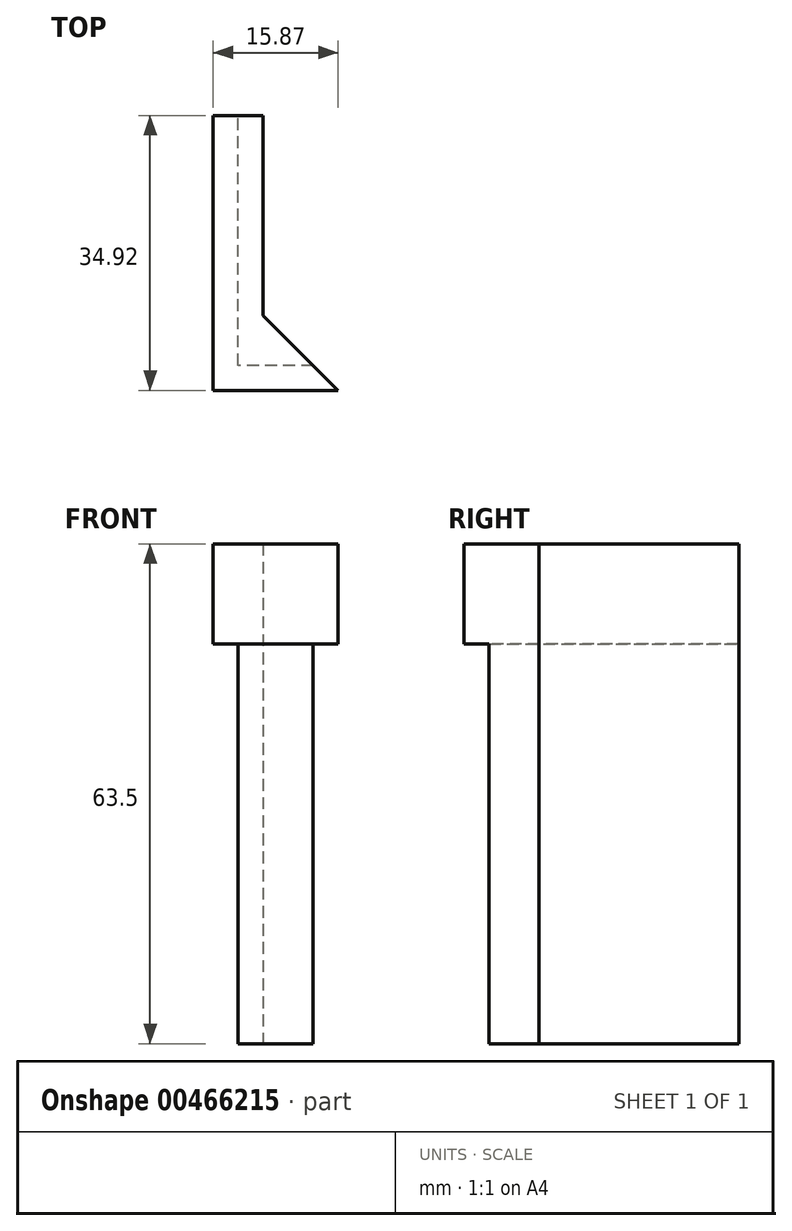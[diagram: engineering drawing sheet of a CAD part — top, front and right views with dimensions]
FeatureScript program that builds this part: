
annotation { "Feature Type Name" : "Feature", "Feature Type Description" : "" }
export const myFeature = defineFeature(function(context is Context, id is Id, definition is map)
    precondition{}
    {
        {
            var Q0;
            Q0=qCreatedBy(makeId("Top.planeOp"),FACE);
            var sketch = newSketch(context, id + "F0", { "sketchPlane" : qUnion([Q0])});
            skLineSegment(sketch, "E0", {"start": v(0, 0) * mm, "end": v(0, 9.52) * mm});
            skLineSegment(sketch, "E1", {"start": v(0, 9.53) * mm, "end": v(9.53, 0) * mm});
            skLineSegment(sketch, "E2", {"start": v(9.52, 0) * mm, "end": v(0, 0) * mm});
            skSolve(sketch);
        }
        {
            var Q0;
            Q0 = qSketchRegion(id + "F0", true);
            extrude(context, id + "F1", {"entities" : qUnion([Q0]), "depth" : 63.5 * mm});
        }
        {
            var Q0;
            Q0=makeQuery(id+"F1.opExtrude","CAP_FACE",FACE,{"disambiguationData":[OSD([sQuery(id+"F0.wireOp",EDGE,"E0"),sQuery(id+"F0.wireOp",EDGE,"E1"),sQuery(id+"F0.wireOp",EDGE,"E2")])],"isStart":false});
            var sketch = newSketch(context, id + "F2", { "sketchPlane" : qUnion([Q0])});
            skLineSegment(sketch, "E3", {"start": v(4.76, 4.76) * mm, "end": v(-3.17, 12.7) * mm});
            skLineSegment(sketch, "E4", {"start": v(-3.18, 12.7) * mm, "end": v(-3.17, -3.18) * mm});
            skLineSegment(sketch, "E5", {"start": v(-3.17, -3.18) * mm, "end": v(12.7, -3.18) * mm});
            skLineSegment(sketch, "E6", {"start": v(12.7, -3.17) * mm, "end": v(4.76, 4.76) * mm});
            skSolve(sketch);
        }
        {
            var Q0;
            Q0 = qSketchRegion(id + "F2", true);
            extrude(context, id + "F3", {"entities" : qUnion([Q0]), "operationType" : NewBodyOperationType.ADD, "oppositeDirection" : true, "depth" : 12.7 * mm});
        }
        {
            var Q0;
            Q0=makeQuery(id+"F1.opExtrude","SWEPT_FACE",FACE,{"disambiguationData":[OSD([sQuery(id+"F0.wireOp",EDGE,"E2")])]});
            var sketch = newSketch(context, id + "F4", { "sketchPlane" : qUnion([Q0])});
            skLineSegment(sketch, "E7", {"start": v(0, 0) * mm, "end": v(3.18, 0) * mm});
            skLineSegment(sketch, "E8", {"start": v(3.18, 0) * mm, "end": v(3.17, 63.5) * mm});
            skLineSegment(sketch, "E9", {"start": v(3.17, 63.5) * mm, "end": v(-3.18, 63.5) * mm});
            skLineSegment(sketch, "E10", {"start": v(-3.18, 63.5) * mm, "end": v(-3.18, 50.8) * mm});
            skLineSegment(sketch, "E11", {"start": v(-3.18, 50.8) * mm, "end": v(0, 50.8) * mm});
            skLineSegment(sketch, "E12", {"start": v(0, 50.8) * mm, "end": v(0, 0) * mm});
            skSolve(sketch);
        }
        {
            var Q0;
            Q0 = qSketchRegion(id + "F4", true);
            extrude(context, id + "F5", {"entities" : qUnion([Q0]), "operationType" : NewBodyOperationType.ADD, "oppositeDirection" : true, "depth" : 31.75 * mm});
        }
        {
            var Q0;
            Q0=makeQuery(id+"F1.opExtrude","SWEPT_FACE",FACE,{"disambiguationData":[OSD([sQuery(id+"F0.wireOp",EDGE,"E2")])]});
            var Q1;
            Q1=makeQuery(id+"F5.boolean.opBoolean","MERGE",FACE,{"derivedFrom":[makeQuery(id+"F1.opExtrude","SWEPT_FACE",FACE,{"disambiguationData":[OSD([sQuery(id+"F0.wireOp",EDGE,"E0")])]}),makeQuery(id+"F5.opExtrude","SWEPT_FACE",FACE,{"disambiguationData":[OSD([sQuery(id+"F4.wireOp",EDGE,"E12")])]})]});
            cPlane(context, id + "F6", {"entities" : qUnion([Q0, Q1]), "cplaneType" : CPlaneType.MID_PLANE, "offset" : 25.4 * mm, "width" : 152.4 * mm, "height" : 152.4 * mm});
        }
    });
